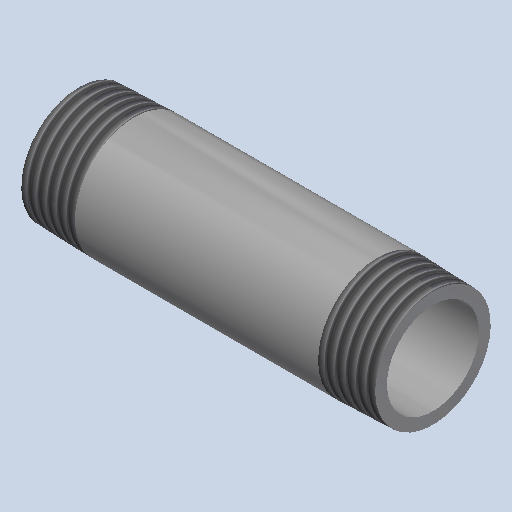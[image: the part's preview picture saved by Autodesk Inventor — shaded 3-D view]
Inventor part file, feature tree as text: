
AUTODESK INVENTOR PART (.ipt)
format: ipt  version: 2025 (Build 290162000, 162)  size: 234,496 bytes
history: native  units: mm (DEFAULTED — no unit token found)
features: other x8, revolve x1
ambient origin geometry x8: Origin, YZ Plane, XZ Plane, XY Plane, X Axis, Y Axis, Z Axis, Center Point
bodies: Solid1 (feature_tree)
feature tree (9):
  revolve  "Revolution1"  [1 undecoded]
  other  "Work Axis1"
  other  "Work Point5"
  other  "Work Axis2"
  other  "Work Point6"
  other  "Work Axis3"
  other  "Work Axis4"
  other  "Work Point7"
  other  "Work Point8"
note: 1 required parameter value undecoded (feature->parameter linkage not recoverable at this tier; creation-order binding heuristic only, values carry confidence <= 0.55)
